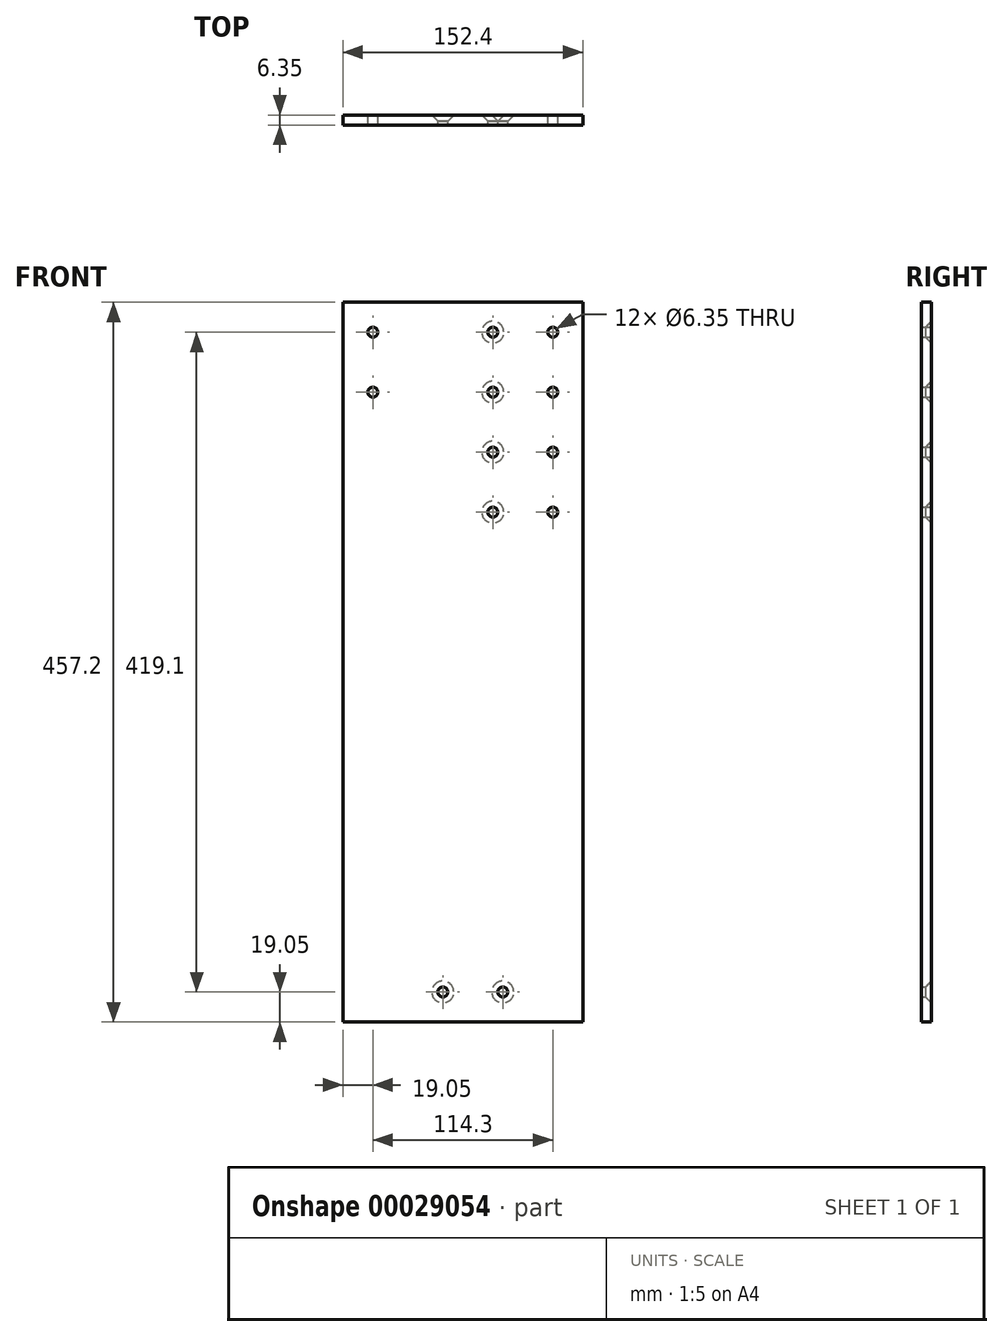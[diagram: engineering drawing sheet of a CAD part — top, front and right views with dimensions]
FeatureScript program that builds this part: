
annotation { "Feature Type Name" : "Feature", "Feature Type Description" : "" }
export const myFeature = defineFeature(function(context is Context, id is Id, definition is map)
    precondition{}
    {
        {
            var Q0;
            Q0=qCreatedBy(makeId("Front.planeOp"),FACE);
            var sketch = newSketch(context, id + "F0", { "sketchPlane" : qUnion([Q0])});
            skLineSegment(sketch, "E0.bottom", {"start": v(0, 0) * mm, "end": v(-152.4, 0) * mm});
            skLineSegment(sketch, "E0.top", {"start": v(0, -457.2) * mm, "end": v(-152.4, -457.2) * mm});
            skLineSegment(sketch, "E0.left", {"start": v(0, 0) * mm, "end": v(0, -457.2) * mm});
            skLineSegment(sketch, "E0.right", {"start": v(-152.4, 0) * mm, "end": v(-152.4, -457.2) * mm});
            skSolve(sketch);
        }
        {
            var Q0;
            Q0 = qSketchRegion(id + "F0", true);
            extrude(context, id + "F1", {"entities" : qUnion([Q0]), "oppositeDirection" : true, "depth" : 6.35 * mm});
        }
        {
            var Q0;
            Q0=makeQuery(id+"F1.opExtrude","CAP_FACE",FACE,{"disambiguationData":[OSD([sQuery(id+"F0.wireOp",EDGE,"E0.bottom"),sQuery(id+"F0.wireOp",EDGE,"E0.top"),sQuery(id+"F0.wireOp",EDGE,"E0.left"),sQuery(id+"F0.wireOp",EDGE,"E0.right")])],"isStart":false});
            var sketch = newSketch(context, id + "F2", { "sketchPlane" : qUnion([Q0])});
            skPoint(sketch, "E1", {"position": v(57.15, -19.05) * mm});
            skPoint(sketch, "E2", {"position": v(57.15, -57.15) * mm});
            skPoint(sketch, "E3", {"position": v(57.15, -95.25) * mm});
            skPoint(sketch, "E4", {"position": v(57.15, -133.35) * mm});
            skPoint(sketch, "E5", {"position": v(19.05, -133.35) * mm});
            skPoint(sketch, "E6", {"position": v(19.05, -95.25) * mm});
            skPoint(sketch, "E7", {"position": v(19.05, -57.15) * mm});
            skPoint(sketch, "E8", {"position": v(19.05, -19.05) * mm});
            skSolve(sketch);
        }
        {
            var Q0;
            Q0=sQuery(id+"F2.wireOp",VERTEX,"E1");
            var Q1;
            Q1=sQuery(id+"F2.wireOp",VERTEX,"E2");
            var Q2;
            Q2=sQuery(id+"F2.wireOp",VERTEX,"E3");
            var Q3;
            Q3=sQuery(id+"F2.wireOp",VERTEX,"E4");
            var Q4;
            Q4=makeQuery(id+"F1.opExtrude","SWEPT_BODY",BODY,{"disambiguationData":[OSD([sQuery(id+"F0.wireOp",EDGE,"E0.bottom"),sQuery(id+"F0.wireOp",EDGE,"E0.top"),sQuery(id+"F0.wireOp",EDGE,"E0.left"),sQuery(id+"F0.wireOp",EDGE,"E0.right")])]});
            hole(context, id + "F3", {"style" : HoleStyle.C_SINK, "holeDiameter" : 6.35 * mm, "cSinkDiameter" : 13.97 * mm, "endStyle" : HoleEndStyle.THROUGH, "locations" : qUnion([Q0, Q1, Q2, Q3]), "scope" : qUnion([Q4]), "cSinkAngle" : 90 * degree});
        }
        {
            var Q0;
            Q0=makeQuery(id+"F1.opExtrude","CAP_FACE",FACE,{"disambiguationData":[OSD([sQuery(id+"F0.wireOp",EDGE,"E0.bottom"),sQuery(id+"F0.wireOp",EDGE,"E0.top"),sQuery(id+"F0.wireOp",EDGE,"E0.left"),sQuery(id+"F0.wireOp",EDGE,"E0.right")])],"isStart":false});
            var sketch = newSketch(context, id + "F4", { "sketchPlane" : qUnion([Q0])});
            skPoint(sketch, "E9", {"position": v(133.35, -19.05) * mm});
            skPoint(sketch, "E10", {"position": v(133.35, -57.15) * mm});
            skSolve(sketch);
        }
        {
            var Q0;
            Q0=sQuery(id+"F4.wireOp",VERTEX,"E9");
            var Q1;
            Q1=sQuery(id+"F4.wireOp",VERTEX,"E10");
            var Q2;
            Q2=makeQuery(id+"F1.opExtrude","SWEPT_BODY",BODY,{"disambiguationData":[OSD([sQuery(id+"F0.wireOp",EDGE,"E0.bottom"),sQuery(id+"F0.wireOp",EDGE,"E0.top"),sQuery(id+"F0.wireOp",EDGE,"E0.left"),sQuery(id+"F0.wireOp",EDGE,"E0.right")])]});
            hole(context, id + "F5", {"style" : HoleStyle.SIMPLE, "holeDiameter" : 6.35 * mm, "endStyle" : HoleEndStyle.THROUGH, "locations" : qUnion([Q0, Q1]), "scope" : qUnion([Q2])});
        }
        {
            var Q0;
            Q0=makeQuery(id+"F1.opExtrude","CAP_FACE",FACE,{"disambiguationData":[OSD([sQuery(id+"F0.wireOp",EDGE,"E0.bottom"),sQuery(id+"F0.wireOp",EDGE,"E0.top"),sQuery(id+"F0.wireOp",EDGE,"E0.left"),sQuery(id+"F0.wireOp",EDGE,"E0.right")])],"isStart":false});
            var sketch = newSketch(context, id + "F6", { "sketchPlane" : qUnion([Q0])});
            skPoint(sketch, "E11", {"position": v(50.8, -438.15) * mm});
            skPoint(sketch, "E12", {"position": v(88.9, -438.15) * mm});
            skSolve(sketch);
        }
        {
            var Q0;
            Q0=sQuery(id+"F6.wireOp",VERTEX,"E11");
            var Q1;
            Q1=sQuery(id+"F6.wireOp",VERTEX,"E12");
            var Q2;
            Q2=makeQuery(id+"F1.opExtrude","SWEPT_BODY",BODY,{"disambiguationData":[OSD([sQuery(id+"F0.wireOp",EDGE,"E0.bottom"),sQuery(id+"F0.wireOp",EDGE,"E0.top"),sQuery(id+"F0.wireOp",EDGE,"E0.left"),sQuery(id+"F0.wireOp",EDGE,"E0.right")])]});
            hole(context, id + "F7", {"style" : HoleStyle.C_SINK, "holeDiameter" : 6.35 * mm, "cSinkDiameter" : 13.97 * mm, "endStyle" : HoleEndStyle.THROUGH, "locations" : qUnion([Q0, Q1]), "scope" : qUnion([Q2]), "cSinkAngle" : 90 * degree});
        }
        {
            var Q0;
            Q0=sQuery(id+"F2.wireOp",VERTEX,"E5");
            var Q1;
            Q1=sQuery(id+"F2.wireOp",VERTEX,"E6");
            var Q2;
            Q2=sQuery(id+"F2.wireOp",VERTEX,"E7");
            var Q3;
            Q3=sQuery(id+"F2.wireOp",VERTEX,"E8");
            var Q4;
            Q4=makeQuery(id+"F1.opExtrude","SWEPT_BODY",BODY,{"disambiguationData":[OSD([sQuery(id+"F0.wireOp",EDGE,"E0.bottom"),sQuery(id+"F0.wireOp",EDGE,"E0.top"),sQuery(id+"F0.wireOp",EDGE,"E0.left"),sQuery(id+"F0.wireOp",EDGE,"E0.right")])]});
            hole(context, id + "F8", {"style" : HoleStyle.SIMPLE, "holeDiameter" : 6.35 * mm, "endStyle" : HoleEndStyle.THROUGH, "locations" : qUnion([Q0, Q1, Q2, Q3]), "scope" : qUnion([Q4])});
        }
    });
